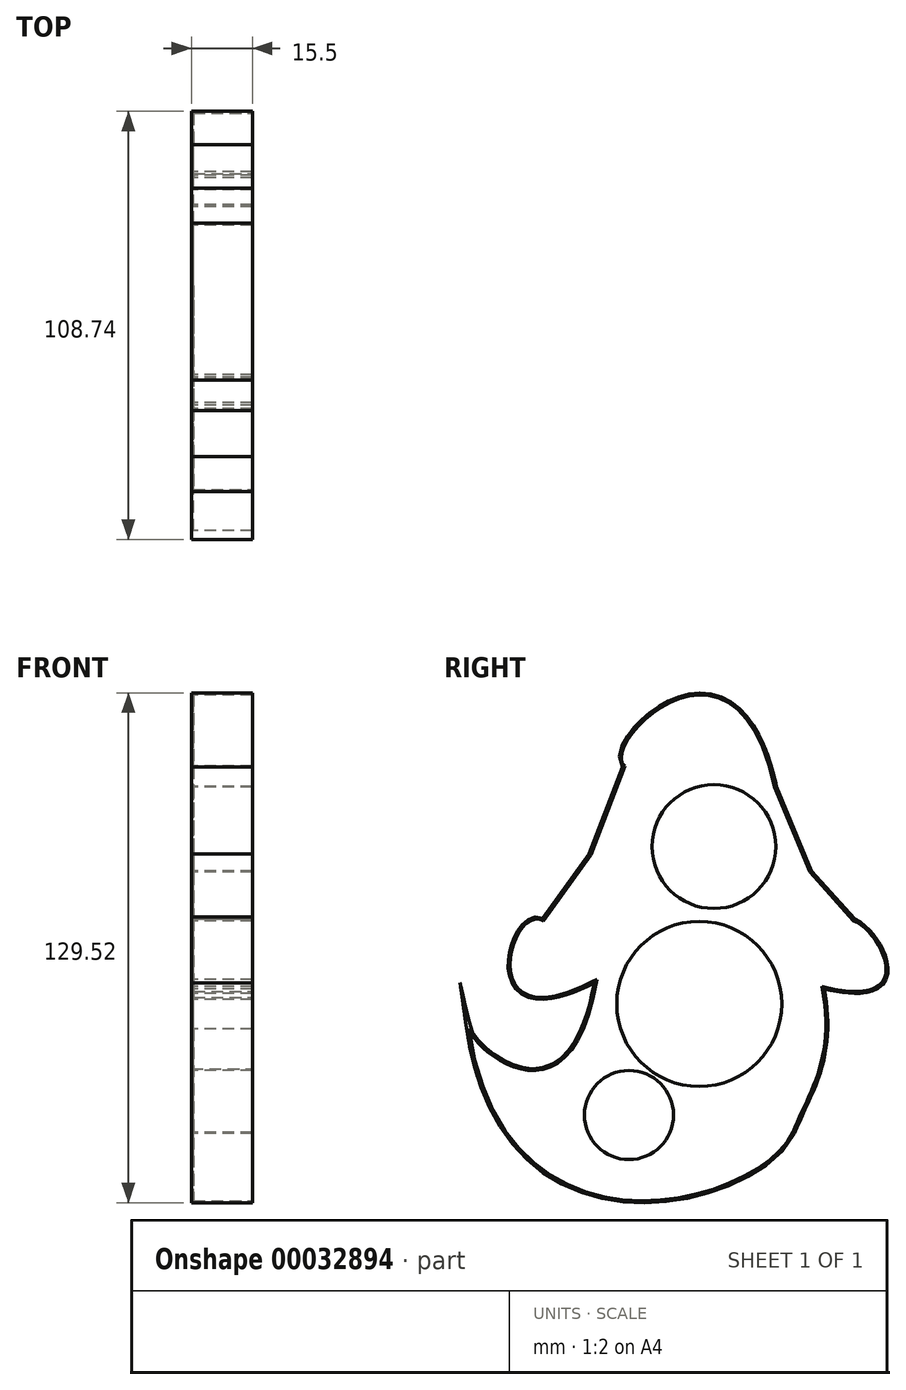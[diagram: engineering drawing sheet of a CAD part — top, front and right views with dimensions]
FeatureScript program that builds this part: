
annotation { "Feature Type Name" : "Feature", "Feature Type Description" : "" }
export const myFeature = defineFeature(function(context is Context, id is Id, definition is map)
    precondition{}
    {
        {
            var Q0;
            Q0=qCreatedBy(makeId("Right.planeOp"),FACE);
            var sketch = newSketch(context, id + "F0", { "sketchPlane" : qUnion([Q0])});
            skLineSegment(sketch, "E0", {"start": v(9.9, 36.64) * mm, "end": v(18.86, 15) * mm});
            skLineSegment(sketch, "E1", {"start": v(-28.14, 41.9) * mm, "end": v(-36.8, 19.33) * mm});
            skFitSpline(sketch, "E2", {"points": [v(-28.14, 41.9) * mm, v(9.9, 36.64) * mm], "startDerivative": vector(-21.12, 16.7) * mm, "endDerivative": vector(29.68, -138.22) * mm});
            skFitSpline(sketch, "E3", {"points": [v(-67.8, -24.88) * mm, v(14.53, -51.18) * mm], "startDerivative": vector(27.35, -188.34) * mm, "endDerivative": vector(24.82, 54.73) * mm});
            skFitSpline(sketch, "E4", {"points": [v(21.95, -14.07) * mm, v(30, 2.63) * mm], "startDerivative": vector(77.23, -19.48) * mm, "endDerivative": vector(-20.65, 7.89) * mm});
            skFitSpline(sketch, "E5", {"points": [v(-48.86, 2.63) * mm, v(-35.25, -12.21) * mm], "startDerivative": vector(-25.76, 14.84) * mm, "endDerivative": vector(95.92, 51.95) * mm});
            skFitSpline(sketch, "E6", {"points": [v(-67.8, -24.88) * mm, v(-35.25, -12.21) * mm], "startDerivative": vector(3.23, -13.94) * mm, "endDerivative": vector(20.2, 119.67) * mm});
            skFitSpline(sketch, "E7", {"points": [v(14.53, -51.18) * mm, v(21.95, -14.07) * mm], "startDerivative": vector(12.3, 31.54) * mm, "endDerivative": vector(-10.44, 55.66) * mm});
            skLineSegment(sketch, "E8", {"start": v(-36.8, 19.33) * mm, "end": v(-48.86, 2.63) * mm});
            skLineSegment(sketch, "E9", {"start": v(18.86, 15) * mm, "end": v(30, 2.63) * mm});
            skSolve(sketch);
        }
        {
            var Q0;
            Q0=makeQuery(id+"F0.imprint","IMPRINT",FACE,{"disambiguationData":[TD([[makeQuery(id+"F0.imprint","IMPRINT",EDGE,{"derivedFrom":sQuery(id+"F0.wireOp",EDGE,"E0")}),-1.0]])]});
            extrude(context, id + "F1", {"entities" : qUnion([Q0]), "depth" : 15 * mm});
        }
        {
            var Q0;
            Q0=makeQuery(id+"F1.opExtrude","CAP_FACE",FACE,{"disambiguationData":[OSD([sQuery(id+"F0.wireOp",EDGE,"E0"),sQuery(id+"F0.wireOp",EDGE,"E1"),sQuery(id+"F0.wireOp",EDGE,"E2"),sQuery(id+"F0.wireOp",EDGE,"E3"),sQuery(id+"F0.wireOp",EDGE,"E4"),sQuery(id+"F0.wireOp",EDGE,"E5"),sQuery(id+"F0.wireOp",EDGE,"E6"),sQuery(id+"F0.wireOp",EDGE,"E7"),sQuery(id+"F0.wireOp",EDGE,"E8"),sQuery(id+"F0.wireOp",EDGE,"E9")])],"isStart":false});
            shell(context, id + "F2", {"entities" : qUnion([Q0]), "thickness" : .5 * mm, "oppositeDirection" : true});
        }
        {
            var Q0;
            Q0=makeQuery(id+"F1.opExtrude","CAP_FACE",FACE,{"disambiguationData":[OSD([sQuery(id+"F0.wireOp",EDGE,"E0"),sQuery(id+"F0.wireOp",EDGE,"E1"),sQuery(id+"F0.wireOp",EDGE,"E2"),sQuery(id+"F0.wireOp",EDGE,"E3"),sQuery(id+"F0.wireOp",EDGE,"E4"),sQuery(id+"F0.wireOp",EDGE,"E5"),sQuery(id+"F0.wireOp",EDGE,"E6"),sQuery(id+"F0.wireOp",EDGE,"E7"),sQuery(id+"F0.wireOp",EDGE,"E8"),sQuery(id+"F0.wireOp",EDGE,"E9")])],"isStart":true});
            var sketch = newSketch(context, id + "F3", { "sketchPlane" : qUnion([Q0])});
            skCircle(sketch, "E10", {"center": v(5.52, 21.48) * mm, "radius": 15.73 * mm});
            skCircle(sketch, "E11", {"center": v(9.25, -18.49) * mm, "radius": 20.96 * mm});
            skCircle(sketch, "E12", {"center": v(27.1, -46.73) * mm, "radius": 11.3 * mm});
            skSolve(sketch);
        }
        {
            var Q0;
            Q0=makeQuery(id+"F3.imprint","IMPRINT",FACE,{"disambiguationData":[TD([[makeQuery(id+"F3.imprint","IMPRINT",EDGE,{"derivedFrom":sQuery(id+"F3.wireOp",EDGE,"E11")}),1.0]])]});
            var Q1;
            Q1=makeQuery(id+"F3.imprint","IMPRINT",FACE,{"disambiguationData":[TD([[makeQuery(id+"F3.imprint","IMPRINT",EDGE,{"derivedFrom":sQuery(id+"F3.wireOp",EDGE,"E10")}),1.0]])]});
            var Q2;
            Q2=makeQuery(id+"F3.imprint","IMPRINT",FACE,{"disambiguationData":[TD([[makeQuery(id+"F3.imprint","IMPRINT",EDGE,{"derivedFrom":sQuery(id+"F3.wireOp",EDGE,"E12")}),1.0]])]});
            extrude(context, id + "F4", {"entities" : qUnion([Q0, Q1, Q2]), "operationType" : NewBodyOperationType.REMOVE, "oppositeDirection" : true, "depth" : 25 * mm});
        }
    });
